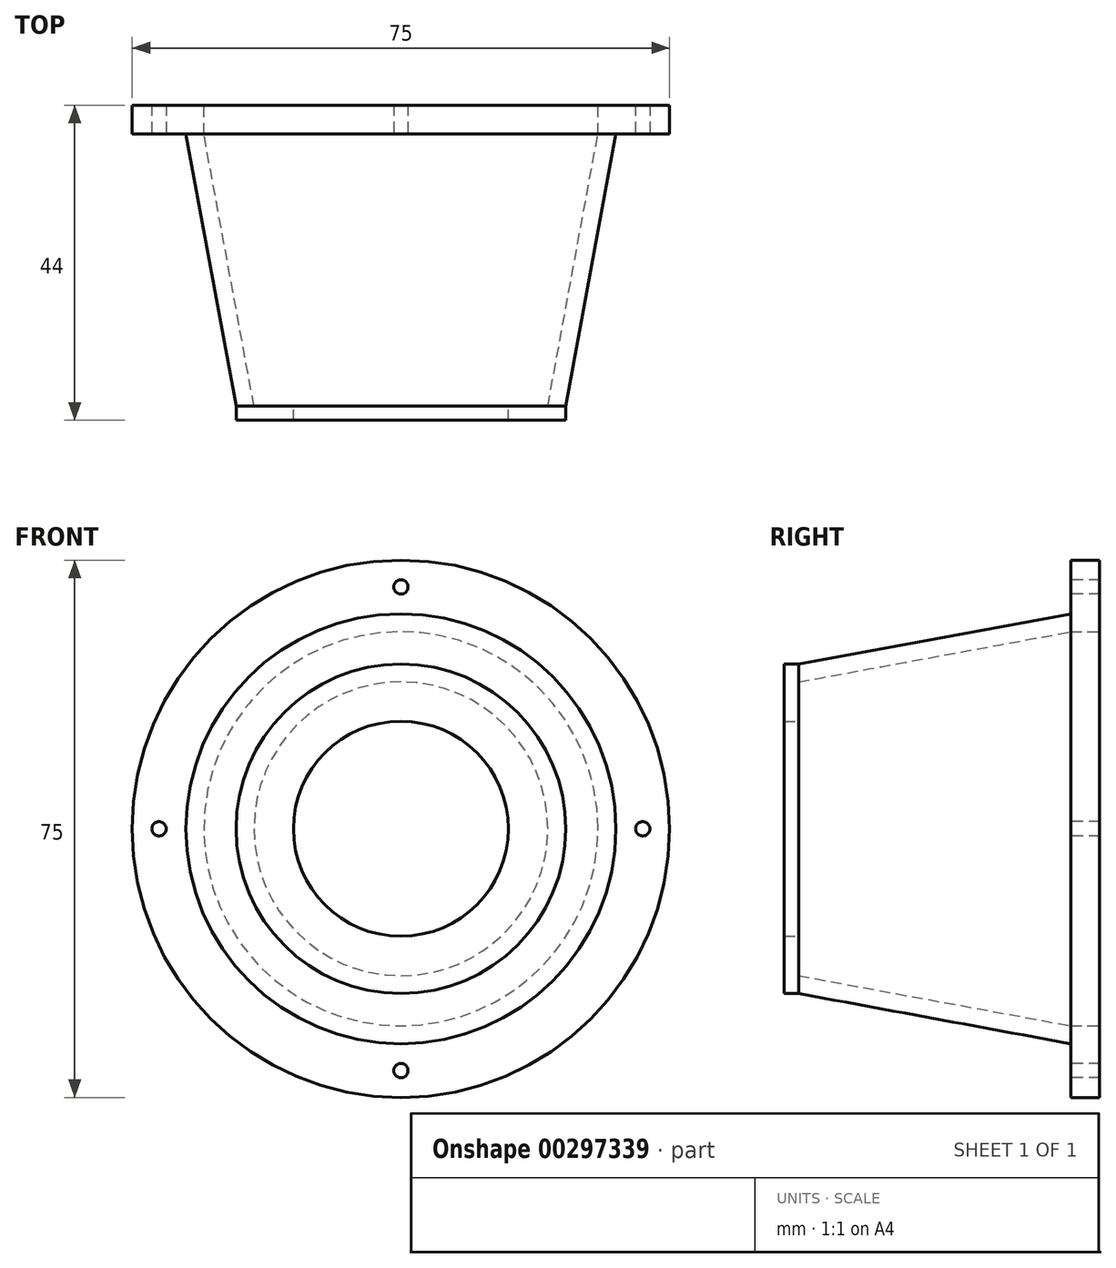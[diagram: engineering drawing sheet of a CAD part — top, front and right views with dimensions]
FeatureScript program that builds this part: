
annotation { "Feature Type Name" : "Feature", "Feature Type Description" : "" }
export const myFeature = defineFeature(function(context is Context, id is Id, definition is map)
    precondition{}
    {
        {
            var Q0;
            Q0=qCreatedBy(makeId("Front.planeOp"),FACE);
            var sketch = newSketch(context, id + "F0", { "sketchPlane" : qUnion([Q0])});
            skCircle(sketch, "E0", {"center": v(0, 0) * mm, "radius": 37.5 * mm});
            skCircle(sketch, "E1", {"center": v(0, 0) * mm, "radius": 30 * mm});
            skSolve(sketch);
        }
        {
            var Q0;
            Q0 = qSketchRegion(id + "F0", true);
            extrude(context, id + "F1", {"entities" : qUnion([Q0]), "depth" : 4 * mm});
        }
        {
            var Q0;
            Q0=makeQuery(id+"F1.opExtrude","CAP_FACE",FACE,{"disambiguationData":[OSD([sQuery(id+"F0.wireOp",EDGE,"E0"),sQuery(id+"F0.wireOp",EDGE,"E1")])],"isStart":false});
            var sketch = newSketch(context, id + "F2", { "sketchPlane" : qUnion([Q0])});
            skCircle(sketch, "E2", {"center": v(0, 0) * mm, "radius": 33.75 * mm, "construction": true});
            skCircle(sketch, "E3", {"center": v(0, 33.75) * mm, "radius": 1 * mm});
            skCircle(sketch, "E4", {"center": v(-33.75, 0) * mm, "radius": 1 * mm});
            skCircle(sketch, "E5", {"center": v(33.75, 0) * mm, "radius": 1 * mm});
            skCircle(sketch, "E6", {"center": v(0, -33.75) * mm, "radius": 1 * mm});
            skSolve(sketch);
        }
        {
            var Q0;
            Q0 = qSketchRegion(id + "F2", true);
            extrude(context, id + "F3", {"entities" : qUnion([Q0]), "operationType" : NewBodyOperationType.REMOVE, "oppositeDirection" : true, "depth" : 25 * mm});
        }
        {
            var Q0;
            Q0=makeQuery(id+"F1.opExtrude","CAP_FACE",FACE,{"disambiguationData":[OSD([sQuery(id+"F0.wireOp",EDGE,"E0"),sQuery(id+"F0.wireOp",EDGE,"E1")])],"isStart":true});
            var sketch = newSketch(context, id + "F4", { "sketchPlane" : qUnion([Q0])});
            skCircle(sketch, "E7", {"center": v(0, 0) * mm, "radius": 30 * mm});
            skCircle(sketch, "E8", {"center": v(0, 0) * mm, "radius": 27.5 * mm});
            skSolve(sketch);
        }
        {
            var Q0;
            Q0 = qSketchRegion(id + "F4", true);
            extrude(context, id + "F5", {"entities" : qUnion([Q0]), "operationType" : NewBodyOperationType.ADD, "oppositeDirection" : true, "depth" : 4 * mm});
        }
        {
            var Q0;
            Q0=makeQuery(id+"F5.boolean.opBoolean","MERGE",FACE,{"derivedFrom":[makeQuery(id+"F1.opExtrude","CAP_FACE",FACE,{"disambiguationData":[OSD([sQuery(id+"F0.wireOp",EDGE,"E0"),sQuery(id+"F0.wireOp",EDGE,"E1")])],"isStart":false}),makeQuery(id+"F5.opExtrude","CAP_FACE",FACE,{"disambiguationData":[OSD([sQuery(id+"F4.wireOp",EDGE,"E7"),sQuery(id+"F4.wireOp",EDGE,"E8")])],"isStart":false})]});
            var sketch = newSketch(context, id + "F6", { "sketchPlane" : qUnion([Q0])});
            skCircle(sketch, "E9", {"center": v(0, 0) * mm, "radius": 30 * mm});
            skSolve(sketch);
        }
        {
            var Q0;
            Q0=qCreatedBy(makeId("Front.planeOp"),FACE);
            cPlane(context, id + "F7", {"entities" : qUnion([Q0]), "cplaneType" : CPlaneType.OFFSET, "offset" : 42 * mm, "width" : 150 * mm, "height" : 150 * mm});
        }
        {
            var Q0;
            Q0=qCreatedBy(id+"F7.planeOp",FACE);
            var sketch = newSketch(context, id + "F8", { "sketchPlane" : qUnion([Q0])});
            skCircle(sketch, "E10", {"center": v(0, 0) * mm, "radius": 23 * mm});
            skSolve(sketch);
        }
        {
            var Q1;
            Q1 = qSketchRegion(id + "F6", true);
            var Q2;
            Q2 = qSketchRegion(id + "F8", true);
            loft(context, id + "F9", {"operationType" : NewBodyOperationType.ADD, "sheetProfilesArray" : [{ "sheetProfileEntities" : qUnion([Q1]) }, { "sheetProfileEntities" : qUnion([Q2]) }]});
        }
        {
            var Q0;
            Q0=makeQuery(id+"F9.opLoft","CAP_FACE",FACE,{"disambiguationData":[OSD([makeQuery(id+"F8.imprint","IMPRINT",FACE,{"disambiguationData":[TD([[makeQuery(id+"F8.imprint","IMPRINT",EDGE,{"derivedFrom":sQuery(id+"F8.wireOp",EDGE,"E10")}),1.0]])]})])],"isStart":true});
            var sketch = newSketch(context, id + "F10", { "sketchPlane" : qUnion([Q0])});
            skCircle(sketch, "E11", {"center": v(0, 0) * mm, "radius": 20.5 * mm});
            skSolve(sketch);
        }
        {
            var Q0;
            Q0=makeQuery(id+"F9.opLoft","CAP_FACE",FACE,{"disambiguationData":[OSD([makeQuery(id+"F6.imprint","IMPRINT",FACE,{"disambiguationData":[TD([[makeQuery(id+"F6.imprint","IMPRINT",EDGE,{"derivedFrom":sQuery(id+"F6.wireOp",EDGE,"E9")}),1.0]])]})])],"isStart":true});
            var sketch = newSketch(context, id + "F11", { "sketchPlane" : qUnion([Q0])});
            skCircle(sketch, "E12", {"center": v(0, 0) * mm, "radius": 27.5 * mm});
            skSolve(sketch);
        }
        {
            var Q1;
            Q1 = qSketchRegion(id + "F11", true);
            var Q2;
            Q2 = qSketchRegion(id + "F10", true);
            loft(context, id + "F12", {"operationType" : NewBodyOperationType.REMOVE, "sheetProfilesArray" : [{ "sheetProfileEntities" : qUnion([Q1]) }, { "sheetProfileEntities" : qUnion([Q2]) }]});
        }
        {
            var Q0;
            Q0=makeQuery(id+"F9.opLoft","CAP_FACE",FACE,{"disambiguationData":[OSD([makeQuery(id+"F8.imprint","IMPRINT",FACE,{"disambiguationData":[TD([[makeQuery(id+"F8.imprint","IMPRINT",EDGE,{"derivedFrom":sQuery(id+"F8.wireOp",EDGE,"E10")}),1.0]])]})])],"isStart":true});
            var sketch = newSketch(context, id + "F13", { "sketchPlane" : qUnion([Q0])});
            skCircle(sketch, "E13", {"center": v(0, 0) * mm, "radius": 23 * mm});
            skCircle(sketch, "E14", {"center": v(0, 0) * mm, "radius": 15 * mm});
            skSolve(sketch);
        }
        {
            var Q0;
            Q0 = qSketchRegion(id + "F13", true);
            extrude(context, id + "F14", {"entities" : qUnion([Q0]), "operationType" : NewBodyOperationType.ADD, "depth" : 2 * mm});
        }
    });
